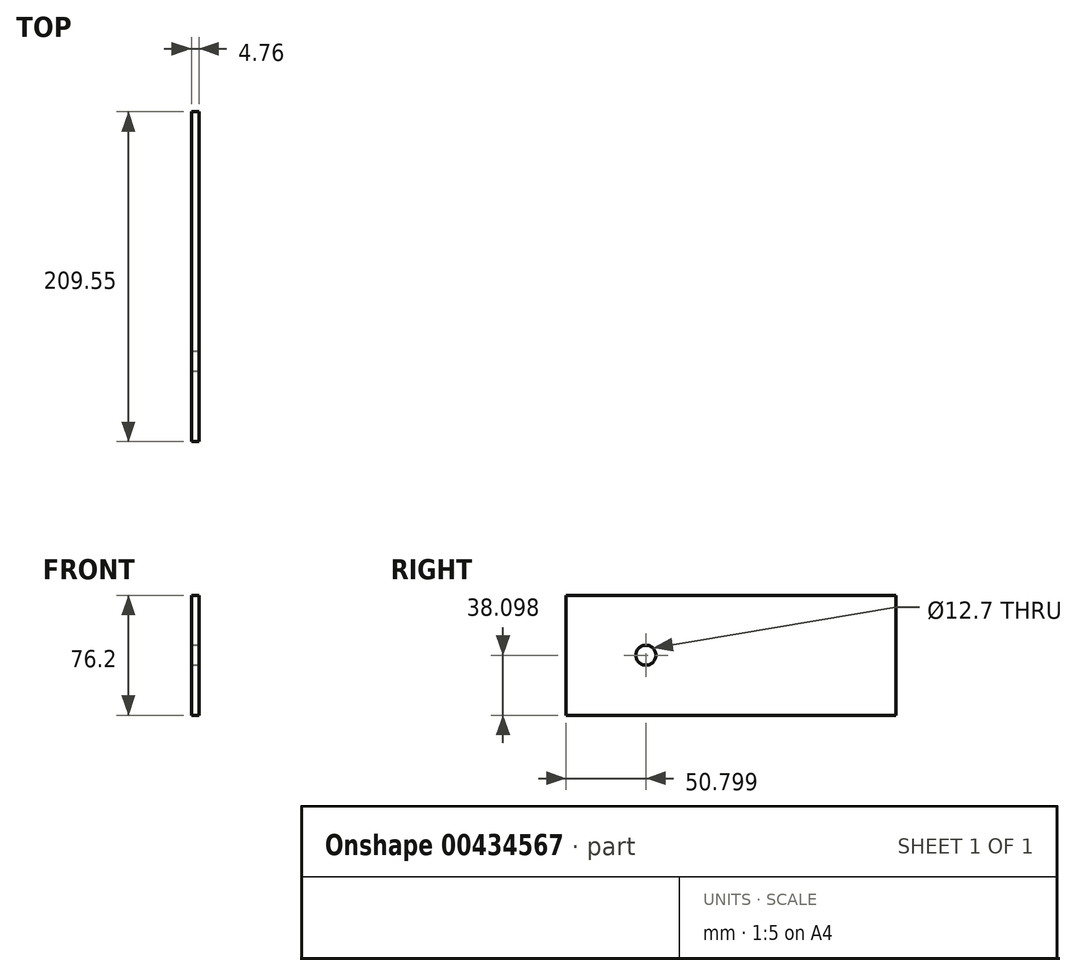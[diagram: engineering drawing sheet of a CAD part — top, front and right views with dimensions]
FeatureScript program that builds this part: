
annotation { "Feature Type Name" : "Feature", "Feature Type Description" : "" }
export const myFeature = defineFeature(function(context is Context, id is Id, definition is map)
    precondition{}
    {
        {
            var Q0;
            Q0=qCreatedBy(makeId("Right.planeOp"),FACE);
            var sketch = newSketch(context, id + "F0", { "sketchPlane" : qUnion([Q0])});
            skLineSegment(sketch, "E0.bottom", {"start": v(-82.61, 48.38) * mm, "end": v(126.94, 48.38) * mm});
            skLineSegment(sketch, "E0.top", {"start": v(-82.61, -27.82) * mm, "end": v(126.94, -27.82) * mm});
            skLineSegment(sketch, "E0.left", {"start": v(-82.61, 48.38) * mm, "end": v(-82.61, -27.82) * mm});
            skLineSegment(sketch, "E0.right", {"start": v(126.94, 48.38) * mm, "end": v(126.94, -27.82) * mm});
            skCircle(sketch, "E1", {"center": v(-31.81, 10.28) * mm, "radius": 6.35 * mm});
            skSolve(sketch);
        }
        {
            var Q0;
            Q0=makeQuery(id+"F0.imprint","IMPRINT",FACE,{"disambiguationData":[TD([[makeQuery(id+"F0.imprint","IMPRINT",EDGE,{"derivedFrom":sQuery(id+"F0.wireOp",EDGE,"E0.bottom")}),-1.0]])]});
            extrude(context, id + "F1", {"entities" : qUnion([Q0]), "depth" : 4.76 * mm});
        }
    });
